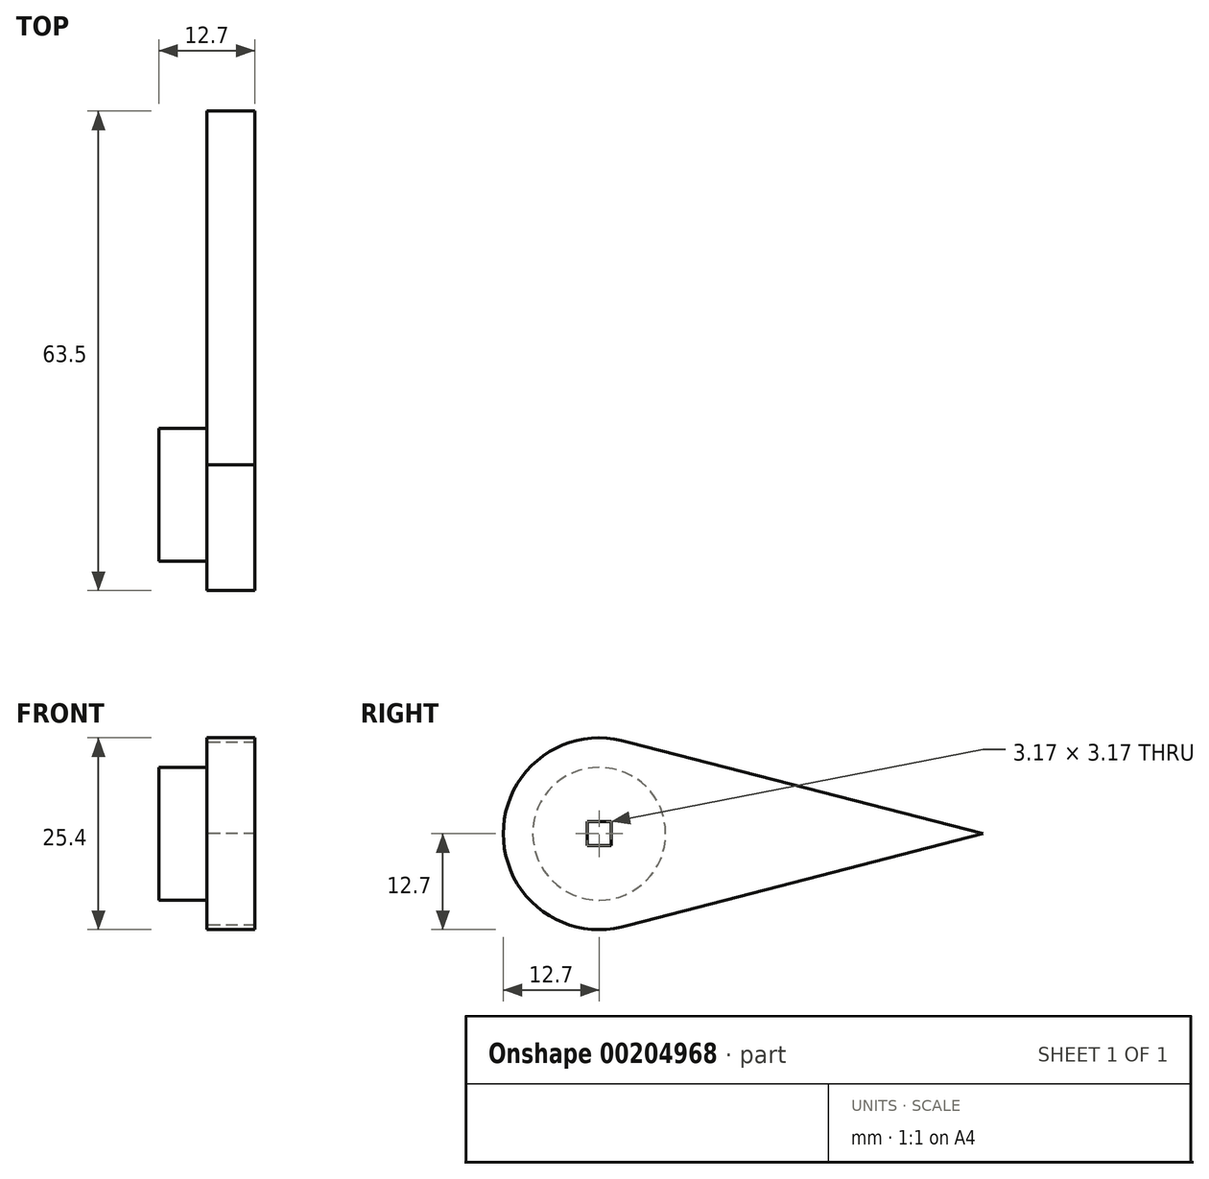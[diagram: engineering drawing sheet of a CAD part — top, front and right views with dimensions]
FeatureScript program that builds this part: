
annotation { "Feature Type Name" : "Feature", "Feature Type Description" : "" }
export const myFeature = defineFeature(function(context is Context, id is Id, definition is map)
    precondition{}
    {
        {
            var Q0;
            Q0=qCreatedBy(makeId("Right.planeOp"),FACE);
            var sketch = newSketch(context, id + "F0", { "sketchPlane" : qUnion([Q0])});
            skArc(sketch, "E0", {"start": v(3.94, 12.07) * mm, "mid": v(-7.46, 10.28) * mm, "end": v(-12.7, 0) * mm});
            skLineSegment(sketch, "E1", {"start": v(3.94, 12.07) * mm, "end": v(50.8, 0) * mm});
            skLineSegment(sketch, "E2", {"start": v(-22.02, 0) * mm, "end": v(63.14, 0) * mm, "construction": true});
            skArc(sketch, "E3.MirrorCS", {"start": v(3.94, -12.07) * mm, "mid": v(-7.46, -10.28) * mm, "end": v(-12.7, 0) * mm});
            skLineSegment(sketch, "E4.MirrorCS", {"start": v(3.94, -12.07) * mm, "end": v(50.8, 0) * mm});
            skSolve(sketch);
        }
        {
            var Q0;
            Q0=makeQuery(id+"F0.imprint","IMPRINT",FACE,{"disambiguationData":[TD([[makeQuery(id+"F0.imprint","IMPRINT",EDGE,{"derivedFrom":sQuery(id+"F0.wireOp",EDGE,"E0")}),1.0]])]});
            extrude(context, id + "F1", {"entities" : qUnion([Q0]), "depth" : 6.35 * mm});
        }
        {
            var Q0;
            Q0=makeQuery(id+"F1.opExtrude","CAP_FACE",FACE,{"disambiguationData":[OSD([sQuery(id+"F0.wireOp",EDGE,"E0"),sQuery(id+"F0.wireOp",EDGE,"E1"),sQuery(id+"F0.wireOp",EDGE,"E3.MirrorCS"),sQuery(id+"F0.wireOp",EDGE,"E4.MirrorCS")])],"isStart":false});
            var sketch = newSketch(context, id + "F2", { "sketchPlane" : qUnion([Q0])});
            skLineSegment(sketch, "E5.bottom", {"start": v(1.59, -1.59) * mm, "end": v(-1.59, -1.59) * mm});
            skLineSegment(sketch, "E5.top", {"start": v(1.59, 1.59) * mm, "end": v(-1.59, 1.59) * mm});
            skLineSegment(sketch, "E5.left", {"start": v(1.59, -1.59) * mm, "end": v(1.59, 1.59) * mm});
            skLineSegment(sketch, "E5.right", {"start": v(-1.59, -1.59) * mm, "end": v(-1.59, 1.59) * mm});
            skPoint(sketch, "E5.middle", {"position": v(0, 0) * mm});
            skSolve(sketch);
        }
        {
            var Q0;
            Q0 = qSketchRegion(id + "F2", true);
            extrude(context, id + "F3", {"entities" : qUnion([Q0]), "operationType" : NewBodyOperationType.REMOVE, "oppositeDirection" : true, "depth" : 25.4 * mm});
        }
        {
            var Q0;
            Q0=qCreatedBy(makeId("Right.planeOp"),FACE);
            var sketch = newSketch(context, id + "F4", { "sketchPlane" : qUnion([Q0])});
            skCircle(sketch, "E6", {"center": v(0, 0) * mm, "radius": 8.8 * mm});
            skLineSegment(sketch, "E7.bottom", {"start": v(-1.59, -1.59) * mm, "end": v(1.59, -1.59) * mm});
            skLineSegment(sketch, "E7.top", {"start": v(-1.59, 1.59) * mm, "end": v(1.59, 1.59) * mm});
            skLineSegment(sketch, "E7.left", {"start": v(-1.59, -1.59) * mm, "end": v(-1.59, 1.59) * mm});
            skLineSegment(sketch, "E7.right", {"start": v(1.59, -1.59) * mm, "end": v(1.59, 1.59) * mm});
            skSolve(sketch);
        }
        {
            var Q0;
            Q0=makeQuery(id+"F4.imprint","IMPRINT",FACE,{"disambiguationData":[TD([[makeQuery(id+"F4.imprint","IMPRINT",EDGE,{"derivedFrom":sQuery(id+"F4.wireOp",EDGE,"E6")}),1.0]])]});
            extrude(context, id + "F5", {"entities" : qUnion([Q0]), "operationType" : NewBodyOperationType.ADD, "oppositeDirection" : true, "depth" : 6.35 * mm});
        }
    });
